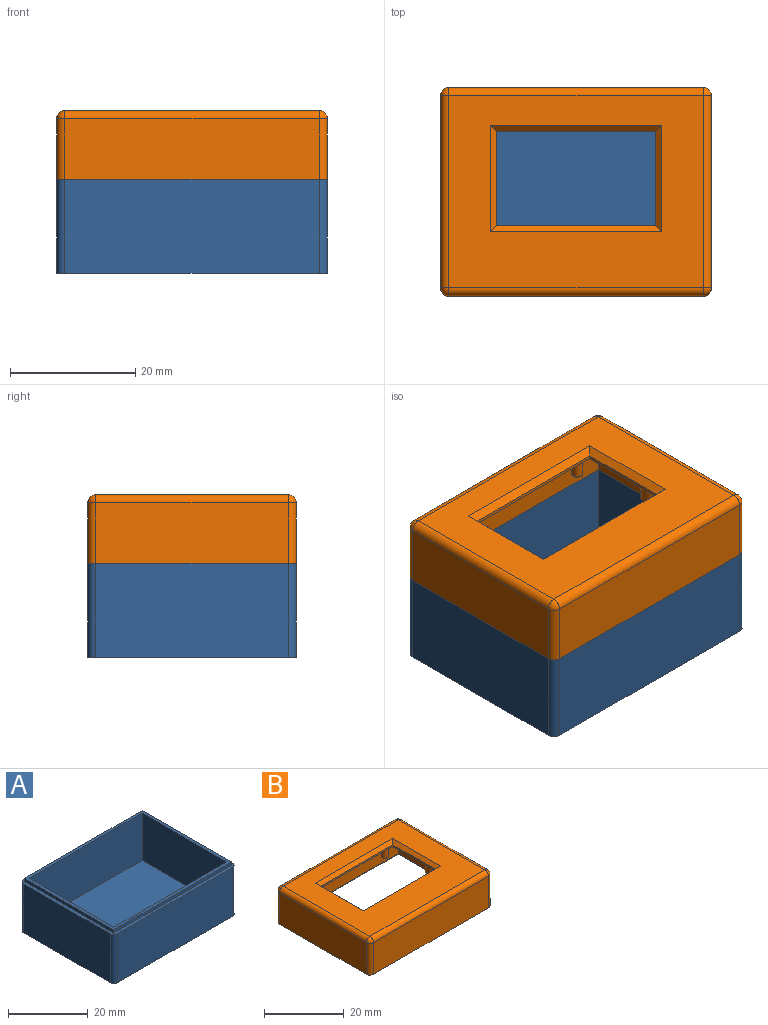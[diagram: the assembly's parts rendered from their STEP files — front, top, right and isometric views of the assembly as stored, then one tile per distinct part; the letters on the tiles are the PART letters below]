
ASSEMBLY  parts=2 mates=1
PART A: 20 faces, bbox 43.3x33.3x16 mm
  f0: plane 30.7x15mm, normal (-1,0,0), area 460.5mm2, adj f4,f5,f16,f19
  f1: plane 40.7x15mm, normal (0,-1,0), area 610.5mm2, adj f4,f5,f16,f17
  f2: plane 30.7x15mm, normal (1,0,0), area 460.5mm2, adj f4,f5,f17,f18
  f3: plane 40.7x15mm, normal (0,1,0), area 610.5mm2, adj f4,f5,f18,f19
  f4: plane 43.3x33.3mm, normal (0,0,1), area 125.9mm2, adj f0,f1,f2,f3,f6,f7,f8,f9
  f5: plane 43.3x33.3mm, normal (0,0,-1), area 1440.4mm2, adj f0,f1,f2,f3,f16,f17,f18,f19
  f6: plane 31.6x1mm, normal (1,0,0), area 31.6mm2, adj f4,f7,f9,f10
  f7: plane 41.6x1mm, normal (0,1,0), area 41.6mm2, adj f4,f6,f8,f10
  f8: plane 31.6x1mm, normal (-1,0,0), area 31.6mm2, adj f4,f7,f9,f10
  f9: plane 41.6x1mm, normal (0,-1,0), area 41.6mm2, adj f4,f6,f8,f10
  f10: plane 41.6x31.6mm, normal (0,0,1), area 114.6mm2, adj f6,f7,f8,f9,f12,f13,f14,f15
  f11: plane 40x30mm, normal (0,0,1), area 1200mm2, adj f12,f13,f14,f15
  f12: plane 30x14.5mm, normal (1,0,0), area 435mm2, adj f10,f11,f13,f15
  f13: plane 40x14.5mm, normal (0,1,0), area 580mm2, adj f10,f11,f12,f14
  f14: plane 30x14.5mm, normal (-1,0,0), area 435mm2, adj f10,f11,f13,f15
  f15: plane 40x14.5mm, normal (0,-1,0), area 580mm2, adj f10,f11,f12,f14
  f16: cylinder r=1.3mm len=15mm, axis (0,0,-1), area 30.6mm2, adj f0,f1,f4,f5
  f17: cylinder r=1.3mm len=15mm, axis (0,0,1), area 30.6mm2, adj f1,f2,f4,f5
  f18: cylinder r=1.3mm len=15mm, axis (0,0,-1), area 30.6mm2, adj f2,f3,f4,f5
  f19: cylinder r=1.3mm len=15mm, axis (0,0,1), area 30.6mm2, adj f0,f3,f4,f5
PART B: 52 faces, bbox 43.3x33.3x11 mm
  f0: plane 40.7x30.7mm, normal (0,0,1), area 782mm2, adj f36,f37,f38,f39,f43,f44,f48,f49
  f1: plane 41.7x31.7mm, normal (0,0,-1), area 121.9mm2, adj f6,f7,f8,f9,f23,f24,f25,f26
  f2: plane 30.7x9.7mm, normal (-1,0,0), area 297.8mm2, adj f27,f42,f48,f51
  f3: plane 40.7x9.7mm, normal (0,-1,0), area 394.8mm2, adj f27,f45,f49,f51
  f4: plane 30.7x9.7mm, normal (1,0,0), area 297.8mm2, adj f27,f40,f44,f45
  f5: plane 40.7x9.7mm, normal (0,1,0), area 394.8mm2, adj f27,f40,f42,f43
  f6: plane 30x8.5mm, normal (1,0,0), area 255mm2, adj f1,f7,f9,f10
  f7: plane 40x8.5mm, normal (0,1,0), area 340mm2, adj f1,f6,f8,f10
  f8: plane 30x8.5mm, normal (-1,0,0), area 255mm2, adj f1,f7,f9,f10
  f9: plane 40x8.5mm, normal (0,-1,0), area 340mm2, adj f1,f6,f8,f10
  f10: plane 40x30mm, normal (0,0,-1), area 783.3mm2, adj f6,f7,f8,f9,f11,f12,f13,f14
  f11: plane 25.5x0.5mm, normal (0,1,0), area 12.8mm2, adj f10,f12,f14,f37
  f12: plane 15x0.5mm, normal (1,0,0), area 7.5mm2, adj f10,f11,f13,f36
  f13: plane 25.5x0.5mm, normal (0,-1,0), area 12.8mm2, adj f10,f12,f14,f38
  f14: plane 15x0.5mm, normal (-1,0,0), area 7.5mm2, adj f10,f11,f13,f39
  f15: cylinder r=0.85mm len=4mm, axis (0,0,1), area 21.4mm2, adj f10,f16
  f16: plane 1.7x1.7mm, normal (0,0,-1), area 2.3mm2, adj f15
  f17: cylinder r=0.85mm len=4mm, axis (0,0,1), area 21.4mm2, adj f10,f18
  f18: plane 1.7x1.7mm, normal (0,0,-1), area 2.3mm2, adj f17
  f19: cylinder r=0.85mm len=4mm, axis (0,0,1), area 21.4mm2, adj f10,f20
  f20: plane 1.7x1.7mm, normal (0,0,-1), area 2.3mm2, adj f19
  f21: cylinder r=0.85mm len=4mm, axis (0,0,1), area 21.4mm2, adj f10,f22
  f22: plane 1.7x1.7mm, normal (0,0,-1), area 2.3mm2, adj f21
  f23: plane 31.7x1mm, normal (1,0,0), area 31.7mm2, adj f1,f24,f26,f27
  f24: plane 41.7x1mm, normal (0,1,0), area 41.7mm2, adj f1,f23,f25,f27
  f25: plane 31.7x1mm, normal (-1,0,0), area 31.7mm2, adj f1,f24,f26,f27
  f26: plane 41.7x1mm, normal (0,-1,0), area 41.7mm2, adj f1,f23,f25,f27
  f27: plane 43.3x33.3mm, normal (0,0,-1), area 118.5mm2, adj f2,f3,f4,f5,f23,f24,f25,f26
  f28: cylinder r=1mm len=5mm, axis (0,0,1), area 31.4mm2, adj f30,f31
  f29: cylinder r=2mm len=5mm, axis (0,0,1), area 62.8mm2, adj f10,f30
  f30: plane 4x4mm, normal (0,0,-1), area 9.4mm2, adj f28,f29
  f31: plane 2x2mm, normal (0,0,-1), area 3.1mm2, adj f28
  f32: cylinder r=1mm len=5mm, axis (0,0,1), area 31.4mm2, adj f34,f35
  f33: cylinder r=2mm len=5mm, axis (0,0,1), area 62.8mm2, adj f10,f34
  f34: plane 4x4mm, normal (0,0,-1), area 9.4mm2, adj f32,f33
  f35: plane 2x2mm, normal (0,0,-1), area 3.1mm2, adj f32
  f36: plane 17x1mm, normal (0.71,0,0.71), area 22.6mm2, adj f0,f12,f37,f38
  f37: plane 27.5x1mm, normal (0,0.71,0.71), area 37.5mm2, adj f0,f11,f36,f39
  f38: plane 27.5x1mm, normal (0,-0.71,0.71), area 37.5mm2, adj f0,f13,f36,f39
  f39: plane 17x1mm, normal (-0.71,0,0.71), area 22.6mm2, adj f0,f14,f37,f38
  f40: cylinder r=1.3mm len=9.7mm, axis (0,0,-1), area 19.8mm2, adj f4,f5,f27,f41
  f41: sphere r=1.3mm, area 2.7mm2, adj f40,f43,f44
  f42: cylinder r=1.3mm len=9.7mm, axis (0,0,1), area 19.8mm2, adj f2,f5,f27,f46
  f43: cylinder r=1.3mm len=40.7mm, axis (1,0,0), area 83.1mm2, adj f0,f5,f41,f46
  f44: cylinder r=1.3mm len=30.7mm, axis (0,-1,0), area 62.7mm2, adj f0,f4,f41,f47
  f45: cylinder r=1.3mm len=9.7mm, axis (0,0,1), area 19.8mm2, adj f3,f4,f27,f47
  f46: sphere r=1.3mm, area 2.7mm2, adj f42,f43,f48
  f47: sphere r=1.3mm, area 2.7mm2, adj f44,f45,f49
  f48: cylinder r=1.3mm len=30.7mm, axis (0,1,0), area 62.7mm2, adj f0,f2,f46,f50
  f49: cylinder r=1.3mm len=40.7mm, axis (-1,0,0), area 83.1mm2, adj f0,f3,f47,f50
  f50: sphere r=1.3mm, area 2.7mm2, adj f48,f49,f51
  f51: cylinder r=1.3mm len=9.7mm, axis (0,0,-1), area 19.8mm2, adj f2,f3,f27,f50
PLACE A t=(-1.54,-0.95,-10.7)mm
PLACE B t=(-1.54,-0.95,5.3)mm
MATE parallel B.f27 <-> A.f4  axis (0,0,-1) through (-1.54,-0.95,4.3)mm
